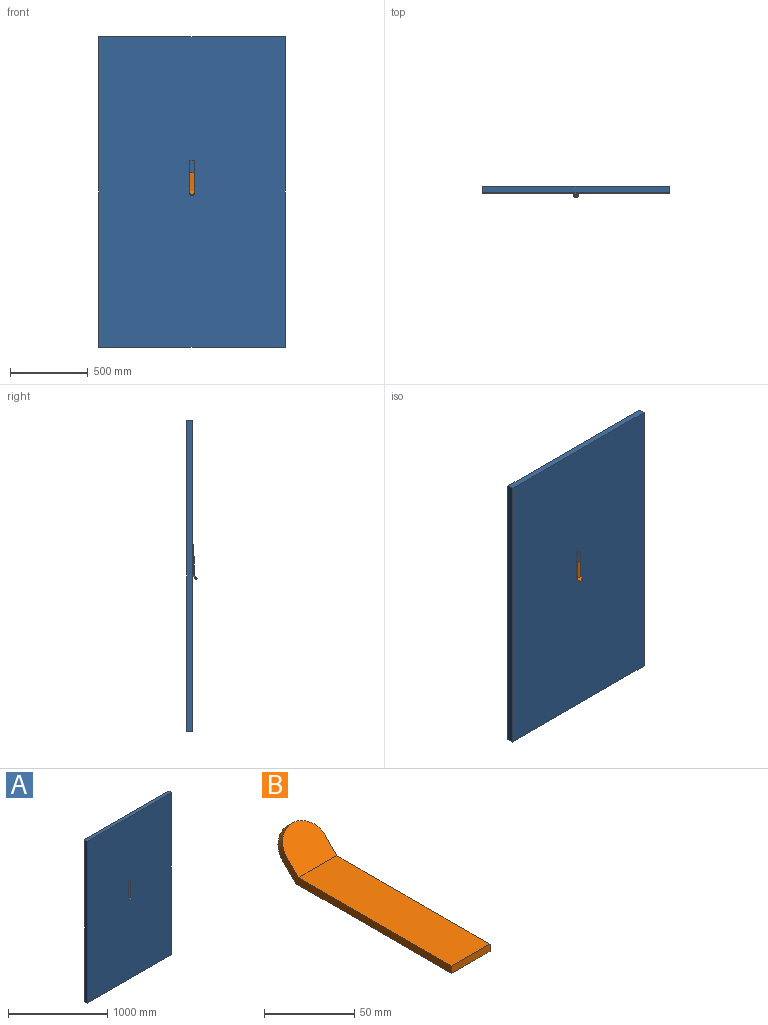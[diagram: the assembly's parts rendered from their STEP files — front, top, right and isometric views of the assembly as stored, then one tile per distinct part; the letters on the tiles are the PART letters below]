
ASSEMBLY  parts=2 mates=1
PART A: 13 faces, bbox 1200x66.2x2000 mm
  f0: plane 2000x40mm, normal (-1,0,0), area 80000mm2, adj f1,f3,f4,f5
  f1: plane 2000x1200mm, normal (0,-1,0), area 2393937.9mm2, adj f0,f2,f4,f5,f6,f9,f10,f11
  f2: plane 2000x40mm, normal (1,0,0), area 80000mm2, adj f1,f3,f4,f5
  f3: plane 2000x1200mm, normal (0,1,0), area 2400000mm2, adj f0,f2,f4,f5
  f4: plane 1200x40mm, normal (0,0,1), area 48000mm2, adj f0,f1,f2,f3
  f5: plane 1200x40mm, normal (0,0,-1), area 48000mm2, adj f0,f1,f2,f3
  f6: plane 30x5mm, normal (0,0,1), area 150mm2, adj f1,f7,f10,f11
  f7: plane 200x30mm, normal (0,-1,0), area 6000mm2, adj f6,f8,f10,f11
  f8: plane 30x21.21mm, normal (0,-0.71,0.71), area 803.4mm2, adj f7,f10,f11,f12
  f9: plane 30x22.68mm, normal (0,0.71,-0.71), area 865.6mm2, adj f1,f10,f11,f12
  f10: plane 214.14x15.61mm, normal (1,0,0), area 1085.4mm2, adj f1,f6,f7,f8,f9,f12
  f11: plane 214.14x15.61mm, normal (-1,0,0), area 1085.4mm2, adj f1,f6,f7,f8,f9,f12
  f12: cylinder r=15mm len=30mm, axis (0,-0.71,0.71), area 235.6mm2, adj f8,f9,f10,f11
PART B: 8 faces, bbox 30x143.3x24.7 mm
  f0: plane 30x21.21mm, normal (0,0.71,-0.71), area 803.4mm2, adj f4,f5,f6,f7
  f1: plane 30x19.75mm, normal (0,-0.71,0.71), area 741.3mm2, adj f2,f5,f6,f7
  f2: plane 120x30mm, normal (0,0,1), area 3600mm2, adj f1,f3,f5,f6
  f3: plane 30x5mm, normal (0,-1,0), area 150mm2, adj f2,f4,f5,f6
  f4: plane 122.07x30mm, normal (0,0,-1), area 3662.1mm2, adj f0,f3,f5,f6
  f5: plane 132.68x14.14mm, normal (1,0,0), area 675mm2, adj f0,f1,f2,f3,f4,f7
  f6: plane 132.68x14.14mm, normal (-1,0,0), area 675mm2, adj f0,f1,f2,f3,f4,f7
  f7: cylinder r=15mm len=30mm, axis (0,0.71,-0.71), area 235.6mm2, adj f0,f1,f5,f6
PLACE A t=(-33.14,-12.74,9.59)mm fixed
PLACE B rot(axis=(0,0.71,-0.71),180deg) t=(-33.14,-36.89,-14.56)mm
MATE revolute A.f12 <-> B.f7  axis (0,-0.71,0.71) through (-33.14,-28.35,1.05)mm
